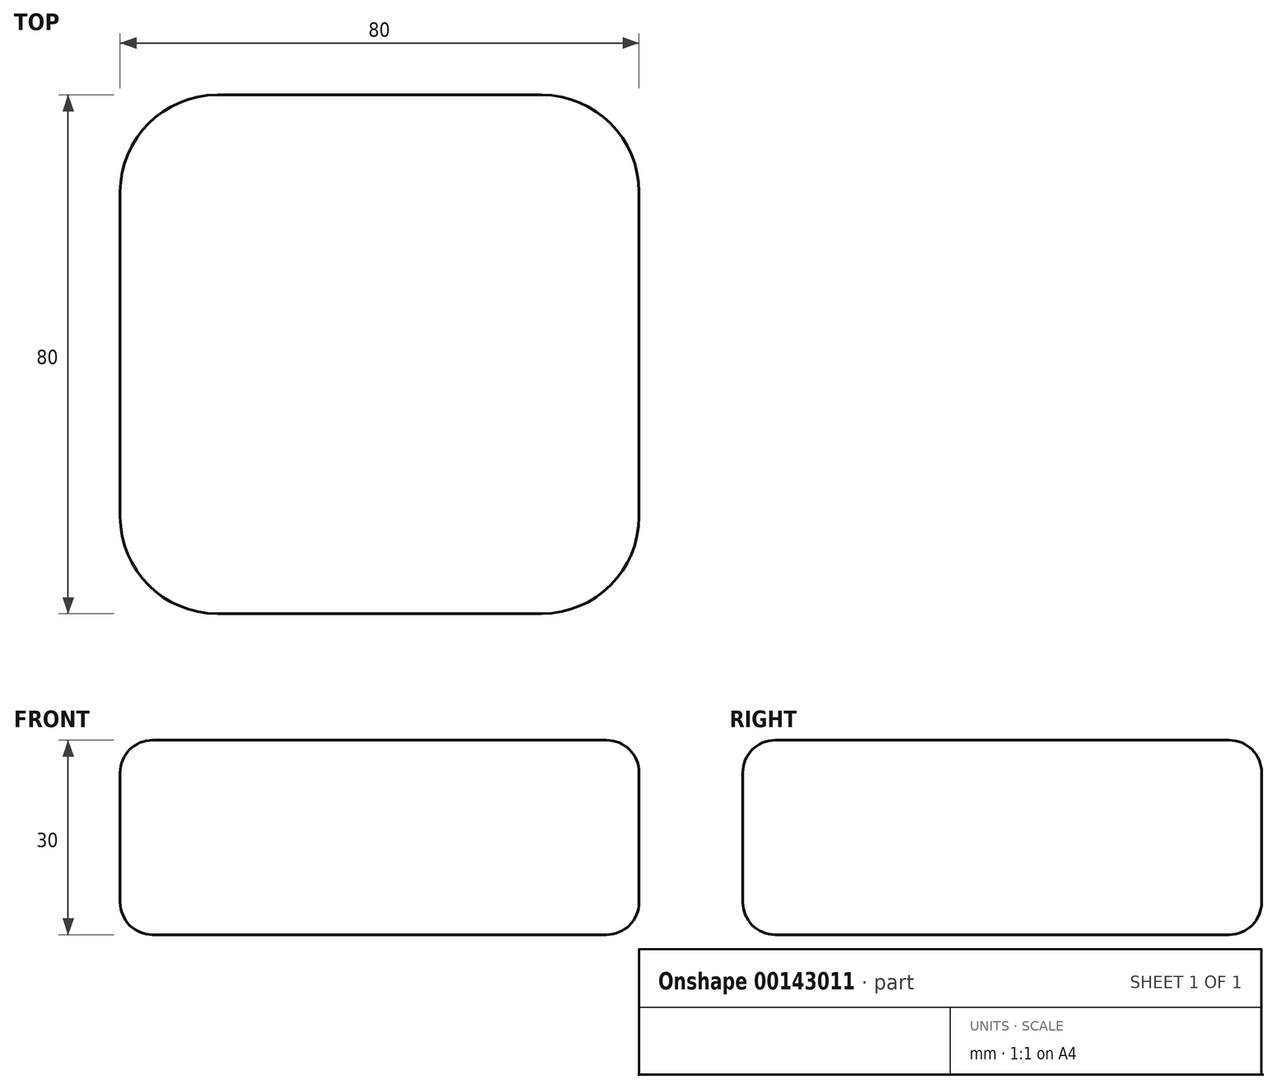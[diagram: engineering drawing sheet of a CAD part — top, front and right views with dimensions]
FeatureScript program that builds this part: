
annotation { "Feature Type Name" : "Feature", "Feature Type Description" : "" }
export const myFeature = defineFeature(function(context is Context, id is Id, definition is map)
    precondition{}
    {
        {
            var Q0;
            Q0=qCreatedBy(makeId("Top.planeOp"),FACE);
            var sketch = newSketch(context, id + "F0", { "sketchPlane" : qUnion([Q0])});
            skLineSegment(sketch, "E0.bottom", {"start": v(15, 0) * mm, "end": v(65, 0) * mm});
            skLineSegment(sketch, "E0.top", {"start": v(15, 80) * mm, "end": v(65, 80) * mm});
            skLineSegment(sketch, "E0.left", {"start": v(0, 15) * mm, "end": v(0, 65) * mm});
            skLineSegment(sketch, "E0.right", {"start": v(80, 15) * mm, "end": v(80, 65) * mm});
            skPoint(sketch, "E1.visualSharp", {"position": v(0, 80) * mm});
            skArc(sketch, "E1.filletArc", {"start": v(15, 80) * mm, "mid": v(4.4, 75.6) * mm, "end": v(0, 65) * mm});
            skPoint(sketch, "E2.visualSharp", {"position": v(0, 0) * mm});
            skArc(sketch, "E2.filletArc", {"start": v(0, 15) * mm, "mid": v(4.4, 4.4) * mm, "end": v(15, 0) * mm});
            skPoint(sketch, "E3.visualSharp", {"position": v(80, 80) * mm});
            skArc(sketch, "E3.filletArc", {"start": v(80, 65) * mm, "mid": v(75.6, 75.6) * mm, "end": v(65, 80) * mm});
            skPoint(sketch, "E4.visualSharp", {"position": v(80, 0) * mm});
            skArc(sketch, "E4.filletArc", {"start": v(65, 0) * mm, "mid": v(75.6, 4.4) * mm, "end": v(80, 15) * mm});
            skSolve(sketch);
        }
        {
            var Q0;
            Q0=qSketchRegion(id+"F0",true);
            extrude(context, id + "F1", {"entities" : qUnion([Q0]), "depth" : 30 * mm});
        }
        {
            var Q0;
            Q0=makeQuery(id+"F1.opExtrude","CAP_FACE",FACE,{"disambiguationData":[OSD([sQuery(id+"F0.wireOp",EDGE,"E0.bottom"),sQuery(id+"F0.wireOp",EDGE,"E0.top"),sQuery(id+"F0.wireOp",EDGE,"E0.left"),sQuery(id+"F0.wireOp",EDGE,"E0.right"),sQuery(id+"F0.wireOp",EDGE,"E1.filletArc"),sQuery(id+"F0.wireOp",EDGE,"E2.filletArc"),sQuery(id+"F0.wireOp",EDGE,"E3.filletArc"),sQuery(id+"F0.wireOp",EDGE,"E4.filletArc")])],"isStart":false});
            var Q1;
            Q1=makeQuery(id+"F1.opExtrude","CAP_FACE",FACE,{"disambiguationData":[OSD([sQuery(id+"F0.wireOp",EDGE,"E0.bottom"),sQuery(id+"F0.wireOp",EDGE,"E0.top"),sQuery(id+"F0.wireOp",EDGE,"E0.left"),sQuery(id+"F0.wireOp",EDGE,"E0.right"),sQuery(id+"F0.wireOp",EDGE,"E1.filletArc"),sQuery(id+"F0.wireOp",EDGE,"E2.filletArc"),sQuery(id+"F0.wireOp",EDGE,"E3.filletArc"),sQuery(id+"F0.wireOp",EDGE,"E4.filletArc")])],"isStart":true});
            fillet(context, id + "F2", {"entities" : qUnion([Q0, Q1]), "radius" : 5 * mm, "tangentPropagation" : true, "allowEdgeOverflow" : false});
        }
    });
